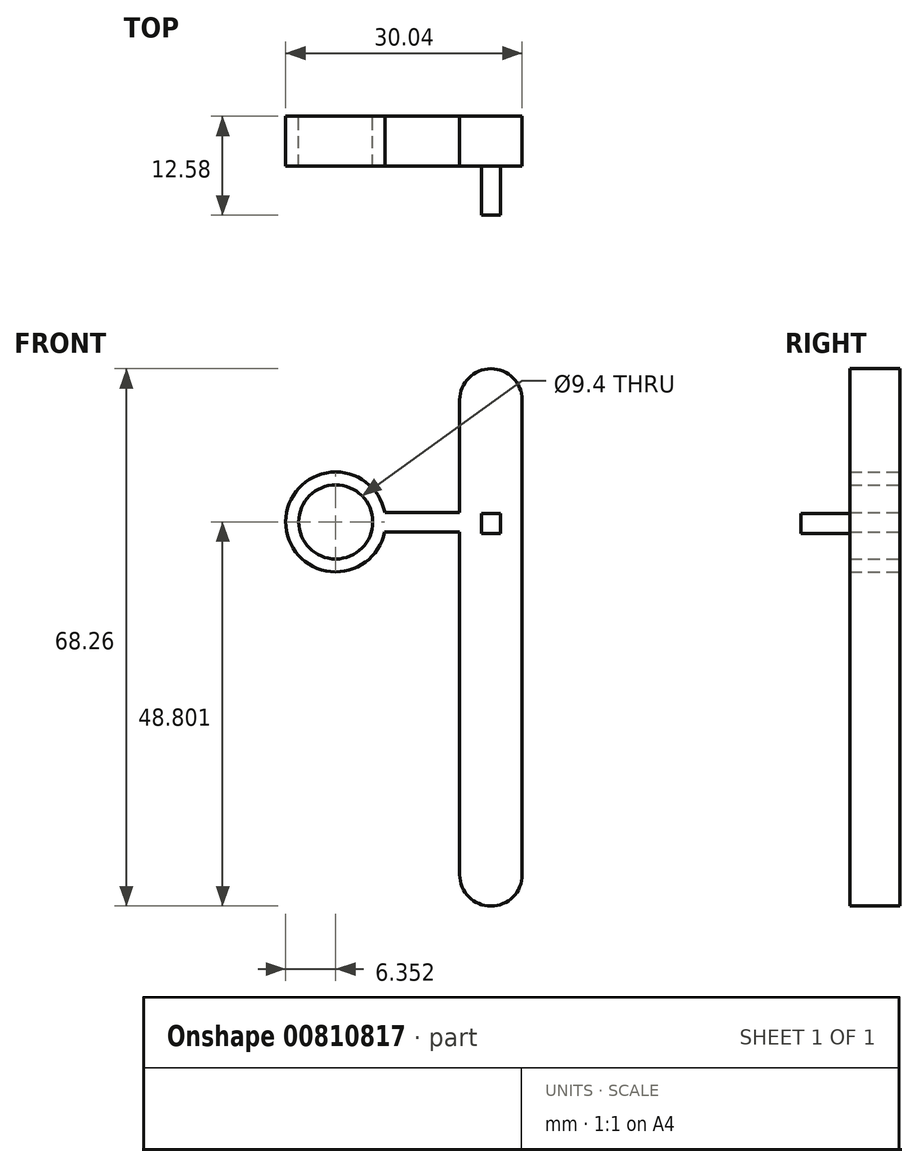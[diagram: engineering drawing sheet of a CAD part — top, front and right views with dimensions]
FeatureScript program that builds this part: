
annotation { "Feature Type Name" : "Feature", "Feature Type Description" : "" }
export const myFeature = defineFeature(function(context is Context, id is Id, definition is map)
    precondition{}
    {
        {
            var Q0;
            Q0=qCreatedBy(makeId("Front.planeOp"),FACE);
            var sketch = newSketch(context, id + "F0", { "sketchPlane" : qUnion([Q0])});
            skLineSegment(sketch, "E0.bottom", {"start": v(3.97, 30.16) * mm, "end": v(-3.97, 30.16) * mm});
            skLineSegment(sketch, "E0.top", {"start": v(3.97, -30.16) * mm, "end": v(-3.97, -30.16) * mm});
            skLineSegment(sketch, "E0.left", {"start": v(3.97, 30.16) * mm, "end": v(3.97, -30.16) * mm});
            skLineSegment(sketch, "E0.right", {"start": v(-3.97, 30.16) * mm, "end": v(-3.97, -30.16) * mm});
            skPoint(sketch, "E0.middle", {"position": v(0, 0) * mm});
            skArc(sketch, "E1", {"start": v(3.97, 30.16) * mm, "mid": v(0, 34.13) * mm, "end": v(-3.97, 30.16) * mm});
            skArc(sketch, "E2", {"start": v(-3.97, -30.16) * mm, "mid": v(0, -34.13) * mm, "end": v(3.97, -30.16) * mm});
            skLineSegment(sketch, "E3", {"start": v(-3.97, 15.87) * mm, "end": v(-13.5, 15.87) * mm});
            skLineSegment(sketch, "E4", {"start": v(-13.5, 15.87) * mm, "end": v(-13.5, 13.41) * mm});
            skLineSegment(sketch, "E5", {"start": v(-13.5, 13.41) * mm, "end": v(-3.97, 13.41) * mm});
            skCircle(sketch, "E6", {"center": v(-19.72, 14.67) * mm, "radius": 6.35 * mm});
            skCircle(sketch, "E7", {"center": v(-19.72, 14.67) * mm, "radius": 4.7 * mm});
            skLineSegment(sketch, "E8.bottom", {"start": v(-1.2, 15.75) * mm, "end": v(1.2, 15.75) * mm});
            skLineSegment(sketch, "E8.top", {"start": v(-1.2, 13.21) * mm, "end": v(1.2, 13.21) * mm});
            skLineSegment(sketch, "E8.left", {"start": v(-1.2, 15.75) * mm, "end": v(-1.2, 13.21) * mm});
            skLineSegment(sketch, "E8.right", {"start": v(1.2, 15.75) * mm, "end": v(1.2, 13.21) * mm});
            skPoint(sketch, "E8.middle", {"position": v(0, 14.48) * mm});
            skSolve(sketch);
        }
        {
            var Q0;
            Q0=makeQuery(id+"F0.imprint","IMPRINT",FACE,{"disambiguationData":[TD([[makeQuery(id+"F0.imprint","IMPRINT",EDGE,{"derivedFrom":sQuery(id+"F0.wireOp",EDGE,"E0.bottom")}),1.0]])]});
            var Q1;
            Q1=makeQuery(id+"F0.imprint","IMPRINT",FACE,{"disambiguationData":[TD([[makeQuery(id+"F0.imprint","IMPRINT",EDGE,{"derivedFrom":sQuery(id+"F0.wireOp",EDGE,"E0.bottom")}),-1.0]])]});
            var Q2;
            Q2=makeQuery(id+"F0.imprint","IMPRINT",FACE,{"disambiguationData":[TD([[makeQuery(id+"F0.imprint","IMPRINT",EDGE,{"derivedFrom":sQuery(id+"F0.wireOp",EDGE,"E0.top")}),1.0]])]});
            var Q3;
            Q3=makeQuery(id+"F0.imprint","IMPRINT",FACE,{"disambiguationData":[TD([[makeQuery(id+"F0.imprint","IMPRINT",EDGE,{"derivedFrom":sQuery(id+"F0.wireOp",EDGE,"E6")}),1.0]])]});
            var Q4;
            {var subQ1=sQuery(id+"F0.wireOp",EDGE,"E0.bottom");Q4=makeQuery(id+"F0.imprint","IMPRINT",FACE,{"disambiguationData":[TD([[makeQuery(id+"F0.imprint","IMPRINT",EDGE,{"derivedFrom":subQ1}),1.0]])]});}
            var Q5;
            {var subQ3=sQuery(id+"F0.wireOp",EDGE,"E3");Q5=makeQuery(id+"F0.imprint","IMPRINT",FACE,{"disambiguationData":[TD([[makeQuery(id+"F0.imprint","IMPRINT",EDGE,{"derivedFrom":subQ3}),1.0]])]});}
            var Q6;
            {var subQ5=sQuery(id+"F0.wireOp",EDGE,"E4");Q6=makeQuery(id+"F0.imprint","IMPRINT",FACE,{"disambiguationData":[TD([[makeQuery(id+"F0.imprint","IMPRINT",EDGE,{"derivedFrom":subQ5}),-1.0]])]});}
            var Q7;
            {var subQ3=sQuery(id+"F0.wireOp",EDGE,"E5");Q7=makeQuery(id+"F0.imprint","IMPRINT",FACE,{"disambiguationData":[TD([[makeQuery(id+"F0.imprint","IMPRINT",EDGE,{"derivedFrom":subQ3}),1.0]])]});}
            extrude(context, id + "F1", {"entities" : qUnion([Q0, Q1, Q2, Q3, Q4, Q5, Q6, Q7]), "endBound" : BoundingType.SYMMETRIC, "depth" : 6.35 * mm, "offsetDistance" : 25.4 * mm});
        }
        {
            var Q0;
            Q0=makeQuery(id+"F0.imprint","IMPRINT",FACE,{"disambiguationData":[TD([[makeQuery(id+"F0.imprint","IMPRINT",EDGE,{"derivedFrom":sQuery(id+"F0.wireOp",EDGE,"E8.bottom")}),-1.0]])]});
            extrude(context, id + "F2", {"entities" : qUnion([Q0]), "operationType" : NewBodyOperationType.ADD, "depth" : 9.4 * mm, "offsetDistance" : 25.4 * mm});
        }
        {
            var Q0;
            Q0=makeQuery(id+"F0.imprint","IMPRINT",FACE,{"disambiguationData":[TD([[makeQuery(id+"F0.imprint","IMPRINT",EDGE,{"derivedFrom":sQuery(id+"F0.wireOp",EDGE,"E8.bottom")}),-1.0]])]});
            extrude(context, id + "F3", {"entities" : qUnion([Q0]), "operationType" : NewBodyOperationType.ADD, "oppositeDirection" : true, "depth" : 3.17 * mm, "offsetDistance" : 25.4 * mm});
        }
    });
